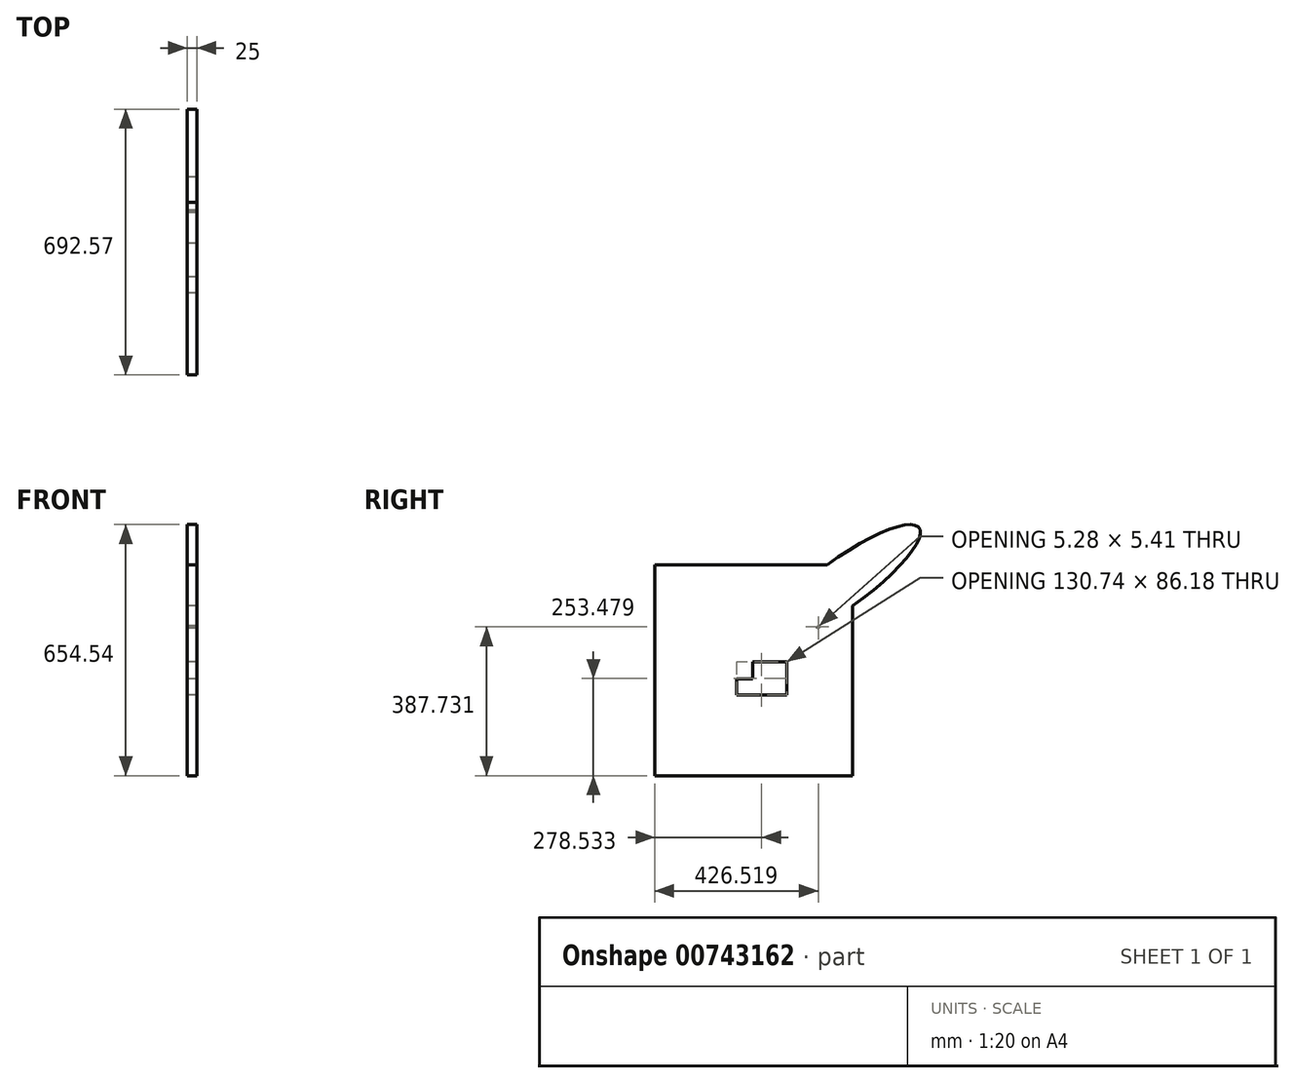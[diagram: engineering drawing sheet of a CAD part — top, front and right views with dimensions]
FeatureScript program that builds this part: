
annotation { "Feature Type Name" : "Feature", "Feature Type Description" : "" }
export const myFeature = defineFeature(function(context is Context, id is Id, definition is map)
    precondition{}
    {
        {
            var Q0;
            Q0=qCreatedBy(makeId("Right.planeOp"),FACE);
            var sketch = newSketch(context, id + "F0", { "sketchPlane" : qUnion([Q0])});
            skEllipse(sketch, "E0", {"center": v(168.2, 172.16) * mm, "majorRadius": 62.96 * mm, "minorRadius": 248.93 * mm, "majorAxis": v(-0.59, 0.8)});
            skLineSegment(sketch, "E1.bottom", {"start": v(24.35, -117.15) * mm, "end": v(-63.8, -117.15) * mm});
            skLineSegment(sketch, "E1.top", {"start": v(24.35, -30.97) * mm, "end": v(-63.8, -30.97) * mm});
            skLineSegment(sketch, "E1.left", {"start": v(24.35, -117.15) * mm, "end": v(24.35, -30.97) * mm});
            skLineSegment(sketch, "E1.right", {"start": v(-63.8, -117.15) * mm, "end": v(-63.8, -30.97) * mm});
            skLineSegment(sketch, "E2.bottom", {"start": v(196.66, 222.46) * mm, "end": v(109.3, 222.46) * mm});
            skLineSegment(sketch, "E2.top", {"start": v(196.66, 125.88) * mm, "end": v(109.3, 125.88) * mm});
            skLineSegment(sketch, "E2.left", {"start": v(196.66, 222.46) * mm, "end": v(196.66, 125.88) * mm});
            skLineSegment(sketch, "E2.right", {"start": v(109.3, 222.46) * mm, "end": v(109.3, 125.88) * mm});
            skLineSegment(sketch, "E3.bottom", {"start": v(-106.39, -74.55) * mm, "end": v(-63.8, -74.55) * mm});
            skLineSegment(sketch, "E3.top", {"start": v(-106.39, -117.15) * mm, "end": v(-63.8, -117.15) * mm});
            skLineSegment(sketch, "E3.left", {"start": v(-106.39, -74.55) * mm, "end": v(-106.39, -117.15) * mm});
            skLineSegment(sketch, "E3.right", {"start": v(-63.8, -74.55) * mm, "end": v(-63.8, -117.15) * mm});
            skLineSegment(sketch, "E4.bottom", {"start": v(-319.55, -327.54) * mm, "end": v(196.66, -327.54) * mm});
            skLineSegment(sketch, "E4.top", {"start": v(-319.55, 222.46) * mm, "end": v(196.66, 222.46) * mm});
            skLineSegment(sketch, "E4.left", {"start": v(-319.55, -327.54) * mm, "end": v(-319.55, 222.46) * mm});
            skLineSegment(sketch, "E4.right", {"start": v(196.66, -327.54) * mm, "end": v(196.66, 222.46) * mm});
            skLineSegment(sketch, "E5.bottom", {"start": v(-65.32, -227.48) * mm, "end": v(-319.55, -227.48) * mm});
            skLineSegment(sketch, "E5.top", {"start": v(-65.32, -282.36) * mm, "end": v(-319.55, -282.36) * mm});
            skLineSegment(sketch, "E5.left", {"start": v(-65.32, -227.48) * mm, "end": v(-65.32, -282.36) * mm});
            skLineSegment(sketch, "E5.right", {"start": v(-319.55, -227.48) * mm, "end": v(-319.55, -282.36) * mm});
            skLineSegment(sketch, "E6", {"start": v(87.2, -35.54) * mm, "end": v(87.2, -35.54) * mm});
            skLineSegment(sketch, "E7", {"start": v(87.2, -35.54) * mm, "end": v(109.6, 62.9) * mm});
            skLineSegment(sketch, "E8", {"start": v(109.6, 62.9) * mm, "end": v(72.79, 25.18) * mm});
            skLineSegment(sketch, "E9", {"start": v(72.79, 25.18) * mm, "end": v(129.18, -110.67) * mm, "construction": true});
            skLineSegment(sketch, "E10", {"start": v(129.18, -110.67) * mm, "end": v(182.73, -23.71) * mm, "construction": true});
            skLineSegment(sketch, "E11", {"start": v(182.73, -23.71) * mm, "end": v(90.7, -65.42) * mm, "construction": true});
            skLineSegment(sketch, "E12", {"start": v(90.7, -65.42) * mm, "end": v(183.35, -34.2) * mm, "construction": true});
            skLineSegment(sketch, "E13", {"start": v(183.35, -34.2) * mm, "end": v(100.46, -112.65) * mm, "construction": true});
            skSolve(sketch);
        }
        {
            var Q0;
            Q0 = qSketchRegion(id + "F0", true);
            extrude(context, id + "F1", {"entities" : qUnion([Q0]), "depth" : 25 * mm, "offsetDistance" : 25 * mm});
        }
    });
